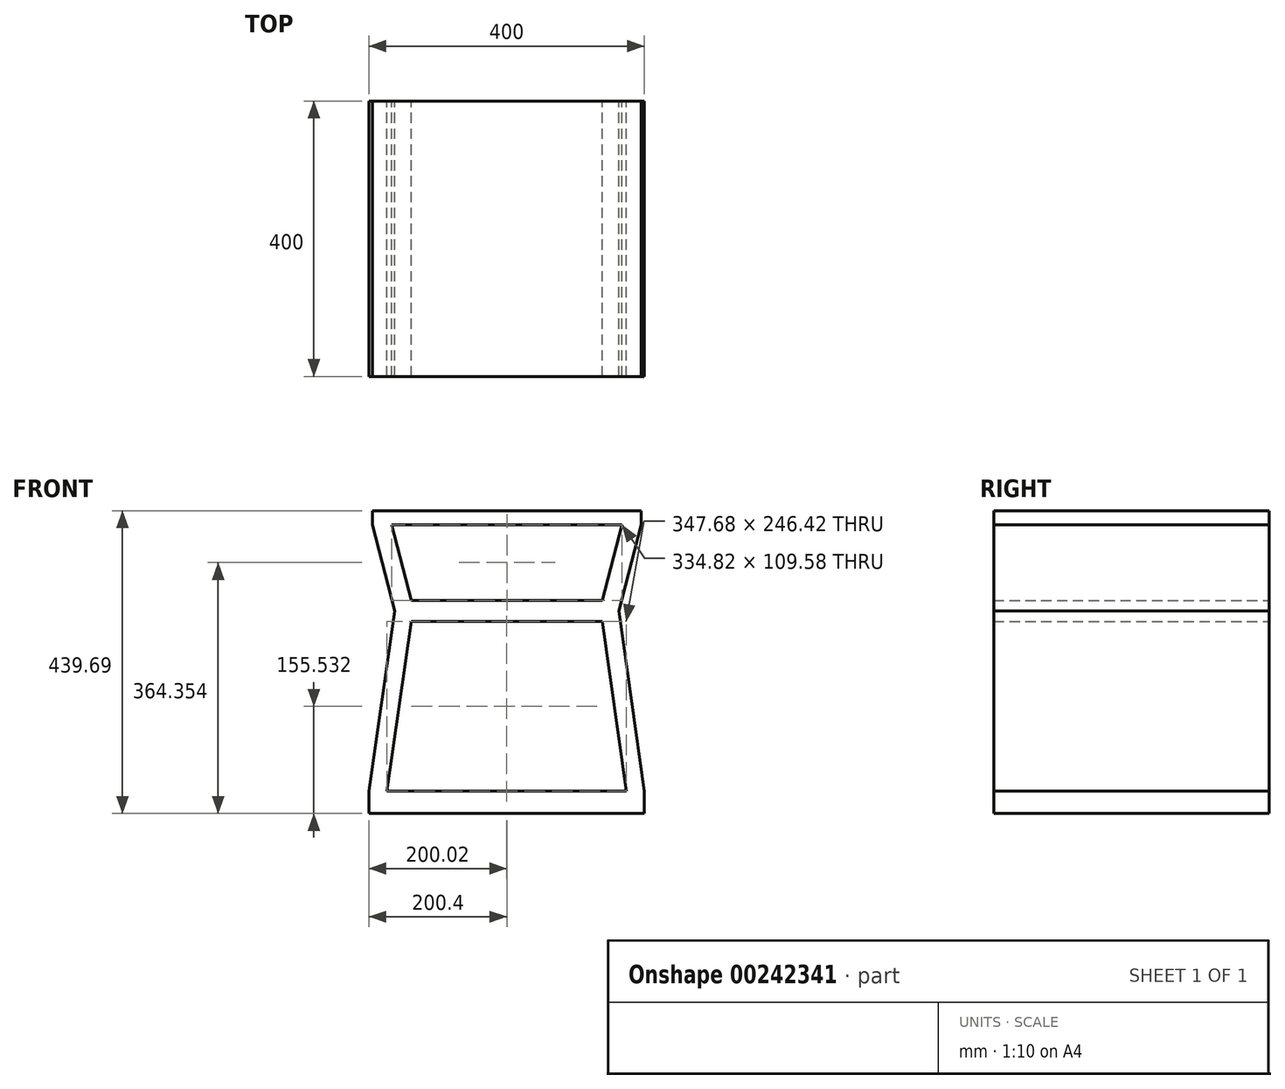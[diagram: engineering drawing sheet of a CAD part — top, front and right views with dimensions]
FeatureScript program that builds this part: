
annotation { "Feature Type Name" : "Feature", "Feature Type Description" : "" }
export const myFeature = defineFeature(function(context is Context, id is Id, definition is map)
    precondition{}
    {
        {
            var Q0;
            Q0=qCreatedBy(makeId("Front.planeOp"),FACE);
            var sketch = newSketch(context, id + "F0", { "sketchPlane" : qUnion([Q0])});
            skLineSegment(sketch, "E0.bottom", {"start": v(-200.4, 0) * mm, "end": v(199.6, 0) * mm});
            skLineSegment(sketch, "E0.top", {"start": v(-174.22, 32.32) * mm, "end": v(173.46, 32.32) * mm});
            skLineSegment(sketch, "E0.left", {"start": v(-200.4, 0) * mm, "end": v(-200.4, 32.32) * mm});
            skLineSegment(sketch, "E0.right", {"start": v(199.6, 0) * mm, "end": v(199.6, 32.32) * mm});
            skLineSegment(sketch, "E1.bottom", {"start": v(167.41, 419.15) * mm, "end": v(-167.41, 419.15) * mm});
            skPoint(sketch, "E1.middle", {"position": v(0, 444.83) * mm});
            skLineSegment(sketch, "E2.bottom", {"start": v(138.9, 278.74) * mm, "end": v(-138.9, 278.74) * mm});
            skLineSegment(sketch, "E2.top", {"start": v(138.9, 309.56) * mm, "end": v(-138.9, 309.56) * mm});
            skPoint(sketch, "E2.middle", {"position": v(0, 294.15) * mm});
            skLineSegment(sketch, "E3", {"start": v(-195.4, 419.15) * mm, "end": v(-162.86, 294.15) * mm});
            skLineSegment(sketch, "E4", {"start": v(162.86, 294.15) * mm, "end": v(195.4, 419.15) * mm});
            skLineSegment(sketch, "E5", {"start": v(162.86, 294.15) * mm, "end": v(199.6, 32.32) * mm});
            skLineSegment(sketch, "E6", {"start": v(-162.86, 294.15) * mm, "end": v(-200.4, 32.32) * mm});
            skLineSegment(sketch, "E7", {"start": v(-138.9, 278.74) * mm, "end": v(-174.22, 32.32) * mm});
            skLineSegment(sketch, "E8", {"start": v(138.9, 278.74) * mm, "end": v(173.46, 32.32) * mm});
            skLineSegment(sketch, "E9", {"start": v(138.9, 309.56) * mm, "end": v(167.41, 419.15) * mm});
            skLineSegment(sketch, "E10", {"start": v(-138.9, 309.56) * mm, "end": v(-167.41, 419.15) * mm});
            skPoint(sketch, "E1.top.end.orphan", {"position": v(-195.4, 470.51) * mm});
            skPoint(sketch, "E1.left.end.orphan", {"position": v(195.4, 470.51) * mm});
            skLineSegment(sketch, "E11", {"start": v(-195.4, 419.15) * mm, "end": v(-195.4, 439.7) * mm});
            skLineSegment(sketch, "E12", {"start": v(-195.4, 439.7) * mm, "end": v(195.4, 439.7) * mm});
            skLineSegment(sketch, "E13", {"start": v(195.4, 439.7) * mm, "end": v(195.4, 419.15) * mm});
            skPoint(sketch, "E14.orphan", {"position": v(-162.86, 309.56) * mm});
            skPoint(sketch, "E2.right.start.orphan", {"position": v(-162.86, 278.74) * mm});
            skPoint(sketch, "E15.orphan", {"position": v(162.86, 278.74) * mm});
            skPoint(sketch, "E2.left.end.orphan", {"position": v(162.86, 309.56) * mm});
            skLineSegment(sketch, "E16", {"start": v(0, 485.91) * mm, "end": v(0, -49.5) * mm});
            skSolve(sketch);
        }
        {
            var Q0;
            Q0=makeQuery(id+"F0.imprint","IMPRINT",FACE,{"disambiguationData":[TD([[makeQuery(id+"F0.imprint","IMPRINT",EDGE,{"derivedFrom":sQuery(id+"F0.wireOp",EDGE,"E0.bottom")}),1.0]])]});
            extrude(context, id + "F1", {"entities" : qUnion([Q0]), "depth" : 200 * mm});
        }
        {
            var Q0;
            Q0=makeQuery(id+"F1.opExtrude","CAP_FACE",FACE,{"disambiguationData":[OSD([sQuery(id+"F0.wireOp",EDGE,"E0.bottom"),sQuery(id+"F0.wireOp",EDGE,"E0.top"),sQuery(id+"F0.wireOp",EDGE,"E0.left"),sQuery(id+"F0.wireOp",EDGE,"E0.right"),sQuery(id+"F0.wireOp",EDGE,"E1.bottom"),sQuery(id+"F0.wireOp",EDGE,"E3"),sQuery(id+"F0.wireOp",EDGE,"E4"),sQuery(id+"F0.wireOp",EDGE,"E5"),sQuery(id+"F0.wireOp",EDGE,"E6"),sQuery(id+"F0.wireOp",EDGE,"E2.bottom"),sQuery(id+"F0.wireOp",EDGE,"E2.top"),sQuery(id+"F0.wireOp",EDGE,"E7"),sQuery(id+"F0.wireOp",EDGE,"E8"),sQuery(id+"F0.wireOp",EDGE,"E9"),sQuery(id+"F0.wireOp",EDGE,"E10"),sQuery(id+"F0.wireOp",EDGE,"E11"),sQuery(id+"F0.wireOp",EDGE,"E12"),sQuery(id+"F0.wireOp",EDGE,"E13")])],"isStart":true});
            extrude(context, id + "F2", {"entities" : qUnion([Q0]), "operationType" : NewBodyOperationType.ADD, "depth" : 200 * mm});
        }
        {
            var Q0;
            Q0=makeQuery(id+"F2.opExtrude","CAP_FACE",FACE,{"disambiguationData":[OSD([sQuery(id+"F0.wireOp",EDGE,"E0.bottom"),sQuery(id+"F0.wireOp",EDGE,"E0.top"),sQuery(id+"F0.wireOp",EDGE,"E0.left"),sQuery(id+"F0.wireOp",EDGE,"E0.right"),sQuery(id+"F0.wireOp",EDGE,"E1.bottom"),sQuery(id+"F0.wireOp",EDGE,"E3"),sQuery(id+"F0.wireOp",EDGE,"E4"),sQuery(id+"F0.wireOp",EDGE,"E5"),sQuery(id+"F0.wireOp",EDGE,"E6"),sQuery(id+"F0.wireOp",EDGE,"E2.bottom"),sQuery(id+"F0.wireOp",EDGE,"E2.top"),sQuery(id+"F0.wireOp",EDGE,"E7"),sQuery(id+"F0.wireOp",EDGE,"E8"),sQuery(id+"F0.wireOp",EDGE,"E9"),sQuery(id+"F0.wireOp",EDGE,"E10"),sQuery(id+"F0.wireOp",EDGE,"E11"),sQuery(id+"F0.wireOp",EDGE,"E12"),sQuery(id+"F0.wireOp",EDGE,"E13")])],"isStart":false});
            var sketch = newSketch(context, id + "F3", { "sketchPlane" : qUnion([Q0])});
            skLineSegment(sketch, "E17", {"start": v(-195.4, 419.15) * mm, "end": v(195.4, 419.15) * mm});
            skSolve(sketch);
        }
    });
